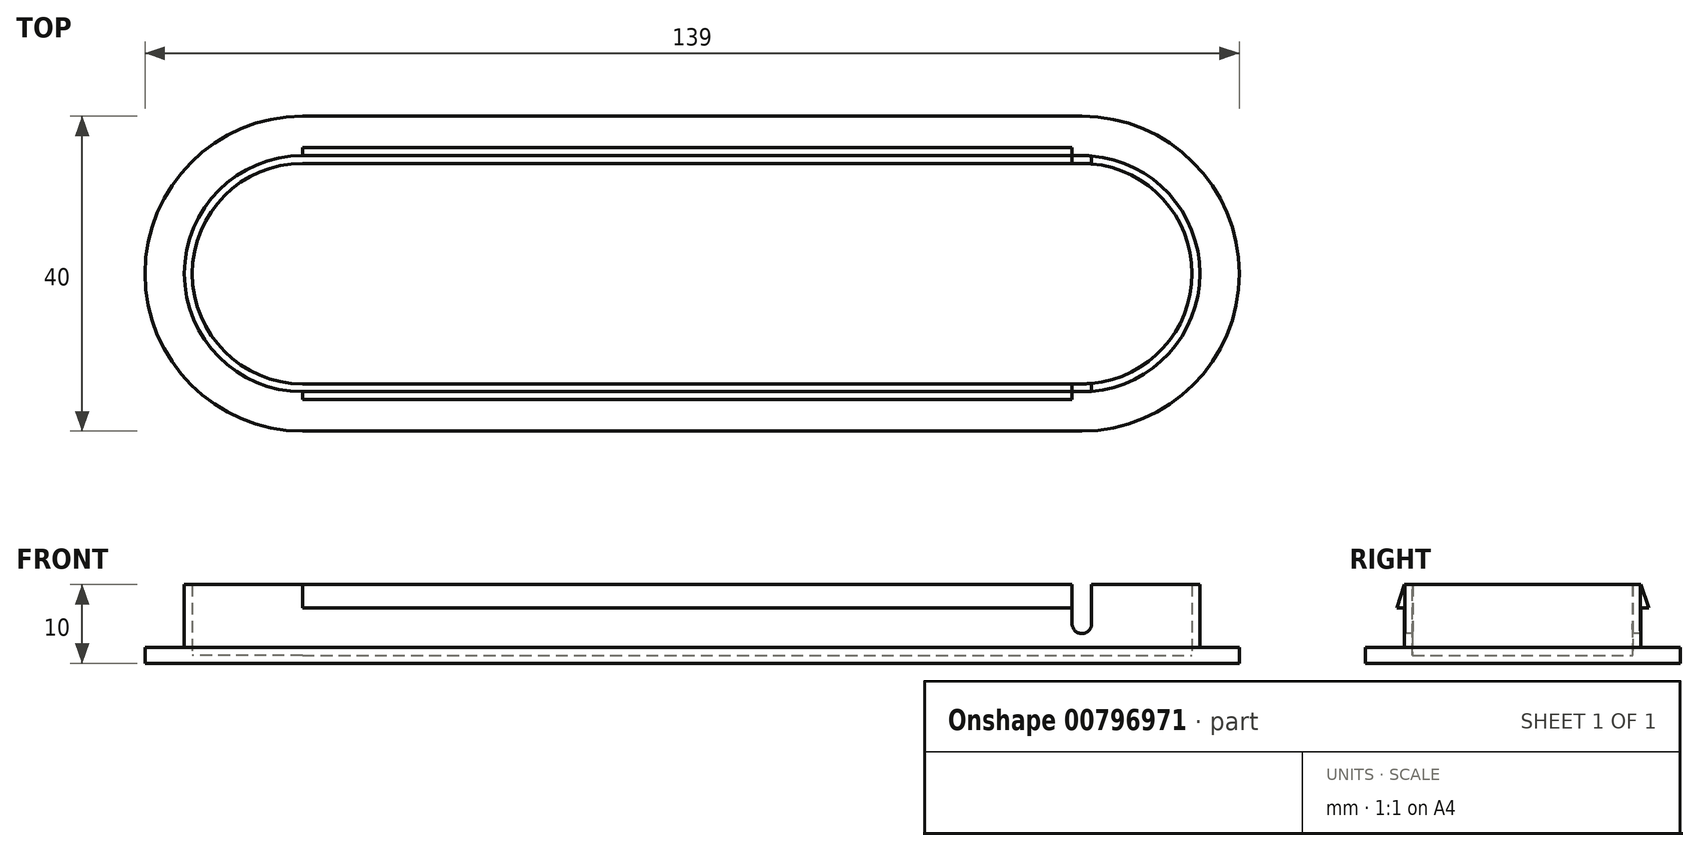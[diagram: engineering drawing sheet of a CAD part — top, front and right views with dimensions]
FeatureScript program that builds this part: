
annotation { "Feature Type Name" : "Feature", "Feature Type Description" : "" }
export const myFeature = defineFeature(function(context is Context, id is Id, definition is map)
    precondition{}
    {
        {
            var Q0;
            Q0=qCreatedBy(makeId("Top.planeOp"),FACE);
            var sketch = newSketch(context, id + "F0", { "sketchPlane" : qUnion([Q0])});
            skArc(sketch, "E0", {"start": v(0, -15) * mm, "mid": v(15, 0) * mm, "end": v(0, 15) * mm});
            skLineSegment(sketch, "E1", {"start": v(15, 0) * mm, "end": v(-114, 0) * mm, "construction": true});
            skArc(sketch, "E2", {"start": v(-99, 15) * mm, "mid": v(-114, 0) * mm, "end": v(-99, -15) * mm});
            skLineSegment(sketch, "E3", {"start": v(-99, 0) * mm, "end": v(-99, 15) * mm, "construction": true});
            skLineSegment(sketch, "E4", {"start": v(-99, 0) * mm, "end": v(-99, -15) * mm, "construction": true});
            skLineSegment(sketch, "E5", {"start": v(0, 0) * mm, "end": v(0, 15) * mm, "construction": true});
            skLineSegment(sketch, "E6", {"start": v(0, 0) * mm, "end": v(0, -15) * mm, "construction": true});
            skLineSegment(sketch, "E7", {"start": v(-99, 15) * mm, "end": v(0, 15) * mm});
            skLineSegment(sketch, "E8", {"start": v(-99, -15) * mm, "end": v(0, -15) * mm});
            skLineSegment(sketch, "E9.0", {"start": v(-99, 20) * mm, "end": v(0, 20) * mm});
            skArc(sketch, "E9.1", {"start": v(-99, 20) * mm, "mid": v(-119, 0) * mm, "end": v(-99, -20) * mm});
            skLineSegment(sketch, "E9.2", {"start": v(-99, -20) * mm, "end": v(0, -20) * mm});
            skArc(sketch, "E9.3", {"start": v(0, -20) * mm, "mid": v(20, 0) * mm, "end": v(0, 20) * mm});
            skSolve(sketch);
        }
        {
            var Q0;
            Q0=makeQuery(id+"F0.imprint","IMPRINT",FACE,{"disambiguationData":[TD([[makeQuery(id+"F0.imprint","IMPRINT",EDGE,{"derivedFrom":sQuery(id+"F0.wireOp",EDGE,"E0")}),-1.0]])]});
            var Q1;
            Q1=makeQuery(id+"F0.imprint","IMPRINT",FACE,{"disambiguationData":[TD([[makeQuery(id+"F0.imprint","IMPRINT",EDGE,{"derivedFrom":sQuery(id+"F0.wireOp",EDGE,"E0")}),1.0]])]});
            extrude(context, id + "F1", {"entities" : qUnion([Q0, Q1]), "oppositeDirection" : true, "depth" : 2 * mm, "offsetDistance" : 25 * mm});
        }
        {
            var Q0;
            Q0=makeQuery(id+"F0.imprint","IMPRINT",FACE,{"disambiguationData":[TD([[makeQuery(id+"F0.imprint","IMPRINT",EDGE,{"derivedFrom":sQuery(id+"F0.wireOp",EDGE,"E0")}),1.0]])]});
            extrude(context, id + "F2", {"entities" : qUnion([Q0]), "operationType" : NewBodyOperationType.ADD, "depth" : 8 * mm, "offsetDistance" : 25 * mm});
        }
        {
            var Q0;
            Q0=makeQuery(id+"F2.opExtrude","CAP_FACE",FACE,{"disambiguationData":[OSD([sQuery(id+"F0.wireOp",EDGE,"E0"),sQuery(id+"F0.wireOp",EDGE,"E2"),sQuery(id+"F0.wireOp",EDGE,"E7"),sQuery(id+"F0.wireOp",EDGE,"E8")])],"isStart":false});
            shell(context, id + "F3", {"entities" : qUnion([Q0]), "thickness" : 1 * mm});
        }
        {
            var Q0;
            Q0=qCreatedBy(makeId("Right.planeOp"),FACE);
            var sketch = newSketch(context, id + "F4", { "sketchPlane" : qUnion([Q0])});
            skLineSegment(sketch, "E10.0", {"start": v(15, 8) * mm, "end": v(15, 0) * mm});
            skLineSegment(sketch, "E11", {"start": v(15, 8) * mm, "end": v(16, 5) * mm});
            skLineSegment(sketch, "E12", {"start": v(16, 5) * mm, "end": v(15, 5) * mm});
            skLineSegment(sketch, "E13", {"start": v(0, 0) * mm, "end": v(0, 14.18) * mm, "construction": true});
            skLineSegment(sketch, "E14.MirrorCS", {"start": v(-15, 8) * mm, "end": v(-15, 0) * mm});
            skLineSegment(sketch, "E15.MirrorCS", {"start": v(-15, 8) * mm, "end": v(-16, 5) * mm});
            skLineSegment(sketch, "E16.MirrorCS", {"start": v(-16, 5) * mm, "end": v(-15, 5) * mm});
            skSolve(sketch);
        }
        {
            var Q0;
            {var subQ0=sQuery(id+"F4.wireOp",EDGE,"E11");Q0=makeQuery(id+"F4.imprint","IMPRINT",FACE,{"disambiguationData":[TD([[makeQuery(id+"F4.imprint","IMPRINT",EDGE,{"derivedFrom":subQ0}),-1.0]])]});}
            var Q1;
            {var subQ0=sQuery(id+"F4.wireOp",EDGE,"E15.MirrorCS");Q1=makeQuery(id+"F4.imprint","IMPRINT",FACE,{"disambiguationData":[TD([[makeQuery(id+"F4.imprint","IMPRINT",EDGE,{"derivedFrom":subQ0}),1.0]])]});}
            var Q2;
            Q2=makeQuery(id+"F2.opExtrude","CAP_EDGE",EDGE,{"disambiguationData":[OSD([sQuery(id+"F0.wireOp",EDGE,"E7")])],"isStart":false});
            sweep(context, id + "F5", {"operationType" : NewBodyOperationType.ADD, "profiles" : qUnion([Q0, Q1]), "path" : qUnion([Q2])});
        }
        {
            var Q0;
            Q0=qCreatedBy(makeId("Front.planeOp"),FACE);
            var sketch = newSketch(context, id + "F6", { "sketchPlane" : qUnion([Q0])});
            skArc(sketch, "E17", {"start": v(-1.24, 3.01) * mm, "mid": v(0, 1.77) * mm, "end": v(1.24, 3.01) * mm});
            skLineSegment(sketch, "E18", {"start": v(-1.24, 3.01) * mm, "end": v(-1.24, 9.2) * mm});
            skLineSegment(sketch, "E19", {"start": v(1.24, 3.01) * mm, "end": v(1.24, 9.87) * mm});
            skLineSegment(sketch, "E20", {"start": v(1.24, 9.87) * mm, "end": v(-1.24, 9.2) * mm});
            skLineSegment(sketch, "E21", {"start": v(0, 0) * mm, "end": v(-99, 0) * mm, "construction": true});
            skLineSegment(sketch, "E22", {"start": v(-49.5, 0) * mm, "end": v(-49.5, 15.63) * mm, "construction": true});
            skArc(sketch, "E23.MirrorCS", {"start": v(-97.76, 3.01) * mm, "mid": v(-99, 1.77) * mm, "end": v(-100.24, 3.01) * mm});
            skLineSegment(sketch, "E24.MirrorCS", {"start": v(-100.24, 9.87) * mm, "end": v(-97.76, 9.2) * mm});
            skLineSegment(sketch, "E25.MirrorCS", {"start": v(-100.24, 3.01) * mm, "end": v(-100.24, 9.87) * mm});
            skLineSegment(sketch, "E26.MirrorCS", {"start": v(-97.76, 3.01) * mm, "end": v(-97.76, 9.2) * mm});
            skSolve(sketch);
        }
        {
            var Q0;
            Q0=makeQuery(id+"F6.imprint","IMPRINT",FACE,{"disambiguationData":[TD([[makeQuery(id+"F6.imprint","IMPRINT",EDGE,{"derivedFrom":sQuery(id+"F6.wireOp",EDGE,"E23.MirrorCS")}),-1.0]])]});
            var Q1;
            Q1=makeQuery(id+"F6.imprint","IMPRINT",FACE,{"disambiguationData":[TD([[makeQuery(id+"F6.imprint","IMPRINT",EDGE,{"derivedFrom":sQuery(id+"F6.wireOp",EDGE,"E17")}),1.0]])]});
            extrude(context, id + "F7", {"entities" : qUnion([Q0, Q1]), "operationType" : NewBodyOperationType.REMOVE, "oppositeDirection" : true, "depth" : 25 * mm, "offsetDistance" : 25 * mm, "hasSecondDirection" : true, "secondDirectionOppositeDirection" : false, "secondDirectionDepth" : 25 * mm});
        }
    });
